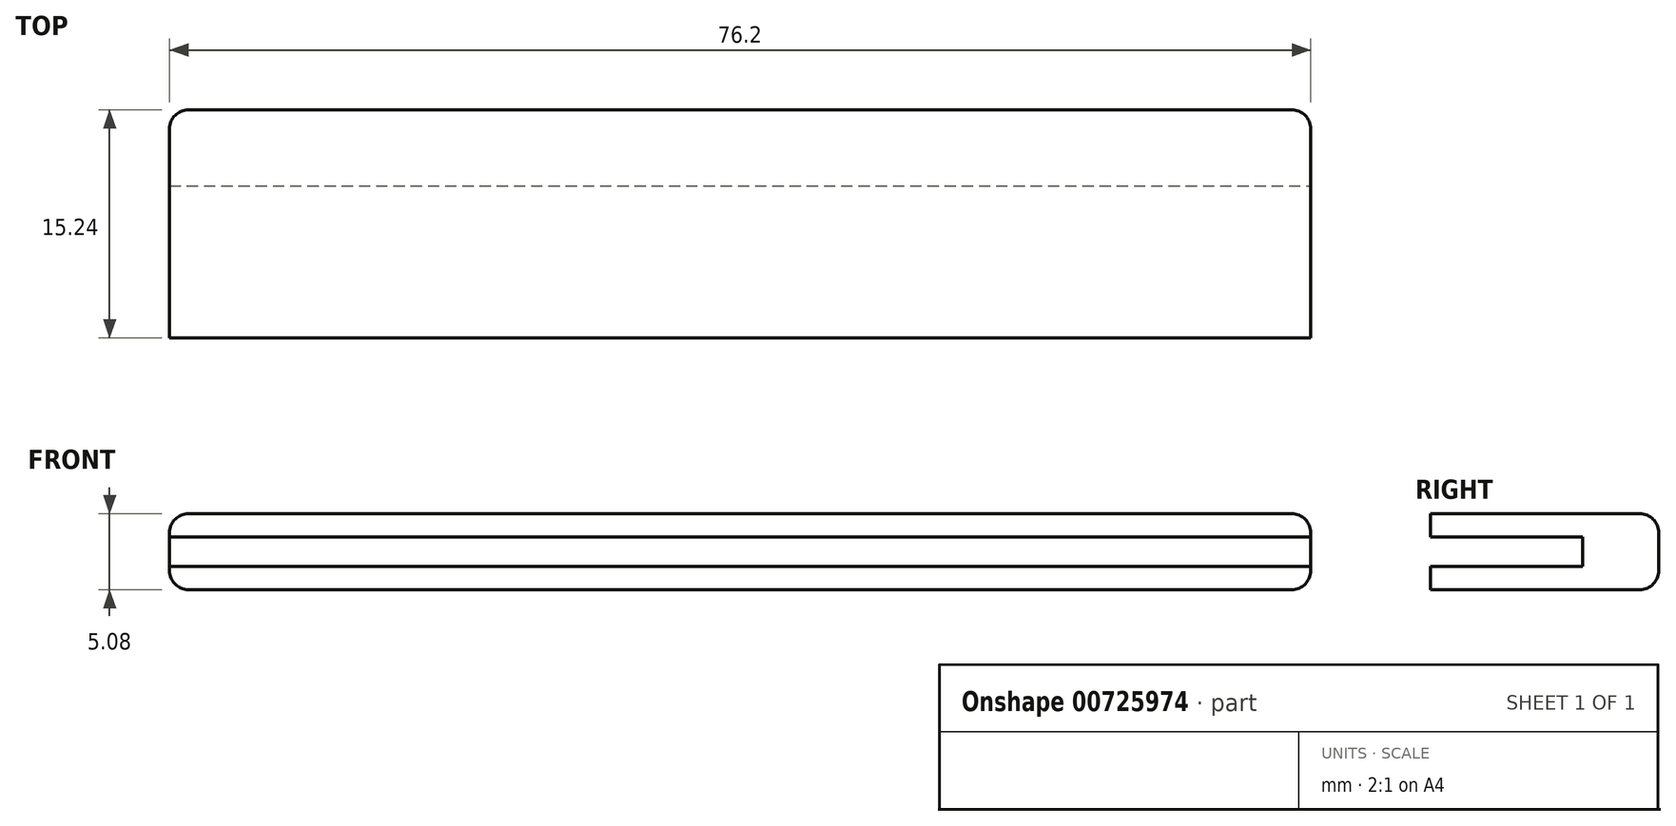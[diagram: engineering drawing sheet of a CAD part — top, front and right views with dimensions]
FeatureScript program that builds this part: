
annotation { "Feature Type Name" : "Feature", "Feature Type Description" : "" }
export const myFeature = defineFeature(function(context is Context, id is Id, definition is map)
    precondition{}
    {
        {
            var Q0;
            Q0=qCreatedBy(makeId("Front.planeOp"),FACE);
            var sketch = newSketch(context, id + "F0", { "sketchPlane" : qUnion([Q0])});
            skLineSegment(sketch, "E0.bottom", {"start": v(-38.1, 5.08) * mm, "end": v(38.1, 5.08) * mm});
            skLineSegment(sketch, "E0.top", {"start": v(-38.1, 0) * mm, "end": v(38.1, 0) * mm});
            skLineSegment(sketch, "E0.left", {"start": v(-38.1, 5.08) * mm, "end": v(-38.1, 0) * mm});
            skLineSegment(sketch, "E0.right", {"start": v(38.1, 5.08) * mm, "end": v(38.1, 0) * mm});
            skPoint(sketch, "E0.middle", {"position": v(0, 2.54) * mm});
            skSolve(sketch);
        }
        {
            var Q0;
            Q0 = qSketchRegion(id + "F0", true);
            extrude(context, id + "F1", {"entities" : qUnion([Q0]), "depth" : 15.24 * mm, "offsetDistance" : 25.4 * mm});
        }
        {
            var Q0;
            Q0=makeQuery(id+"F1.opExtrude","CAP_FACE",FACE,{"disambiguationData":[OSD([sQuery(id+"F0.wireOp",EDGE,"E0.bottom"),sQuery(id+"F0.wireOp",EDGE,"E0.top"),sQuery(id+"F0.wireOp",EDGE,"E0.left"),sQuery(id+"F0.wireOp",EDGE,"E0.right")])],"isStart":false});
            var sketch = newSketch(context, id + "F2", { "sketchPlane" : qUnion([Q0])});
            skLineSegment(sketch, "E1.bottom", {"start": v(-38.1, 3.53) * mm, "end": v(38.1, 3.53) * mm});
            skLineSegment(sketch, "E1.top", {"start": v(-38.1, 1.55) * mm, "end": v(38.1, 1.55) * mm});
            skLineSegment(sketch, "E1.left", {"start": v(-38.1, 3.53) * mm, "end": v(-38.1, 1.55) * mm});
            skLineSegment(sketch, "E1.right", {"start": v(38.1, 3.53) * mm, "end": v(38.1, 1.55) * mm});
            skPoint(sketch, "E1.middle", {"position": v(0, 2.54) * mm});
            skLineSegment(sketch, "E2", {"start": v(-38.1, 2.54) * mm, "end": v(38.1, 2.54) * mm, "construction": true});
            skSolve(sketch);
        }
        {
            var Q0;
            Q0=makeQuery(id+"F2.imprint","IMPRINT",FACE,{"disambiguationData":[TD([[makeQuery(id+"F2.imprint","IMPRINT",EDGE,{"derivedFrom":sQuery(id+"F2.wireOp",EDGE,"E1.bottom")}),-1.0]])]});
            extrude(context, id + "F3", {"entities" : qUnion([Q0]), "operationType" : NewBodyOperationType.REMOVE, "oppositeDirection" : true, "depth" : 10.16 * mm, "offsetDistance" : 25.4 * mm});
        }
        {
            var Q0;
            Q0=makeQuery(id+"F1.opExtrude","CAP_EDGE",EDGE,{"disambiguationData":[OSD([sQuery(id+"F0.wireOp",EDGE,"E0.bottom")])],"isStart":true});
            var Q1;
            Q1=makeQuery(id+"F1.opExtrude","CAP_EDGE",EDGE,{"disambiguationData":[OSD([sQuery(id+"F0.wireOp",EDGE,"E0.top")])],"isStart":true});
            var Q2;
            Q2=makeQuery(id+"F1.opExtrude","CAP_EDGE",EDGE,{"disambiguationData":[OSD([sQuery(id+"F0.wireOp",EDGE,"E0.left")])],"isStart":true});
            var Q3;
            Q3=makeQuery(id+"F1.opExtrude","CAP_EDGE",EDGE,{"disambiguationData":[OSD([sQuery(id+"F0.wireOp",EDGE,"E0.right")])],"isStart":true});
            var Q4;
            Q4=makeQuery(id+"F1.opExtrude","SWEPT_EDGE",EDGE,{"disambiguationData":[OSD([sQuery(id+"F0.wireOp",EDGE,"E0.bottom"),sQuery(id+"F0.wireOp",EDGE,"E0.right")])]});
            var Q5;
            Q5=makeQuery(id+"F1.opExtrude","SWEPT_EDGE",EDGE,{"disambiguationData":[OSD([sQuery(id+"F0.wireOp",EDGE,"E0.top"),sQuery(id+"F0.wireOp",EDGE,"E0.right")])]});
            var Q6;
            Q6=makeQuery(id+"F1.opExtrude","SWEPT_EDGE",EDGE,{"disambiguationData":[OSD([sQuery(id+"F0.wireOp",EDGE,"E0.bottom"),sQuery(id+"F0.wireOp",EDGE,"E0.left")])]});
            var Q7;
            Q7=makeQuery(id+"F1.opExtrude","SWEPT_EDGE",EDGE,{"disambiguationData":[OSD([sQuery(id+"F0.wireOp",EDGE,"E0.top"),sQuery(id+"F0.wireOp",EDGE,"E0.left")])]});
            fillet(context, id + "F4", {"entities" : qUnion([Q0, Q1, Q2, Q3, Q4, Q5, Q6, Q7]), "radius" : 1.27 * mm, "tangentPropagation" : true, "allowEdgeOverflow" : false});
        }
    });
